# Revit family: Heat_Pump-Air_to_Water-Rheem--
name_source: partatom
category: Mechanical Equipment
units: mm (PartAtom-declared; Revit-internal decimal feet)

## family parameters
Always vertical = Yes
Cut with Voids When Loaded = No
OmniClass Number = 23.75.10.21.17
OmniClass Title = Water-Source Heat Pumps
Part Type = Normal
Room Calculation Point = No
Round Connector Dimension = Use Radius
Shared = No
Work Plane-Based = No

## types (1)
- ERROR_LOAD TYPE CATALOG
    Apparent Power = 24000 VA
    Assembly Code = D3040600
    Back Clearance = 850 mm  [stored 2.78871 ft]
    Base Height = 80 mm  [stored 0.262467 ft]
    Connection Size = 65 mm
    DHW Pipe Horizontal Offset = 360 mm  [stored 1.1811 ft]
    DHW Retiurn Pipe Vertical Offset = 300 mm
    DHW Supply Pipe Vertical Offset = 1040 mm  [stored 3.41207 ft]
    Default Elevation = 0 mm  [stored 0 ft]
    Description = Air to Water Heat Pump
    ENGworks Global = www.ENGWorksGlobal.com
    Enclosure Height = 1360 mm  [stored 4.46194 ft]
    Enclosure Length = 2180 mm  [stored 7.15223 ft]
    Enclosure Material = Metal - Rheem - Gray
    Enclosure Width = 1135 mm  [stored 3.72375 ft]
    Fan Height = 40 mm  [stored 0.131234 ft]
    Fan Radius = 200 mm  [stored 0.656168 ft]
    Flange Diameter = 185 mm  [stored 0.606955 ft]
    Flange Radius = 93 mm
    Flange Thickness = 18 mm  [stored 0.0590551 ft]
    Frequency = 50 Hz
    Front Clearance = 500 mm  [stored 1.64042 ft]
    Heat Exchanger Type = 316 Stainless Steel Double Wall Brazed Plates
    Hot Water Flow = 3.6 L/s
    Left Clearance = 1000 mm  [stored 3.28084 ft]
    Load Classification = HVAC
    Load Sub-Classification Motor = Yes
    Manufacturer = Rheem
    Maximum DHW Temperature = 65 °C
    Maximum Overcurrent Protection = 41 A
    Minimum Circuit Amps = 50 A
    Model = 953060DP
    Nominal Heating Capacity = 60720 W
    Number of Poles = 1
    Phase = 1
    Pipe Diameter = 122 mm  [stored 0.400262 ft]
    Pipe Length = 140 mm
    Power Consumption = 14 kW
    Product Page URL = https://www.rheem.com.au
    Refrigerant Used = R134a
    Right Clearance = 1000 mm  [stored 3.28084 ft]
    System Performance COP = 4.42
    Top Clearance = 3500 mm  [stored 11.4829 ft]
    URL = https://www.rheem.com.au
    Unit Weight = 450.00 kgf
    Unit Weight Value = 450
    Version = 1
    Voltage = 480 V
    Voltage Comments = 380 VAC - 415 VAC

note: [stored X ft] marks values corroborated as IEEE doubles in the binary element streams (Revit-internal decimal feet)

## geometry (parser evidence)
native form markers: Sweep x6
no freeform markers — native parametric forms only
